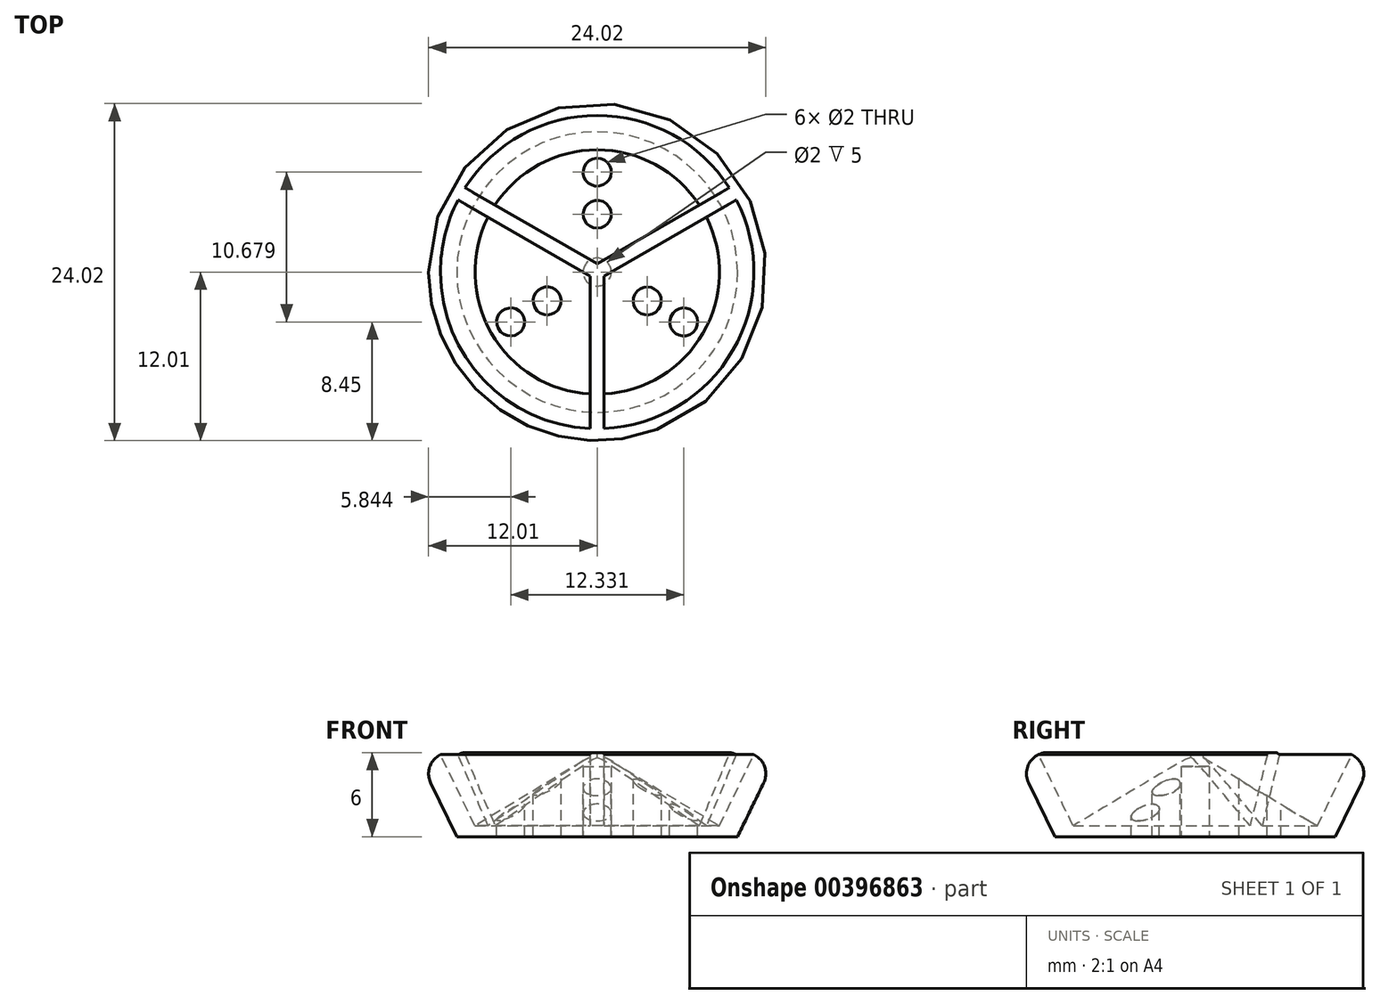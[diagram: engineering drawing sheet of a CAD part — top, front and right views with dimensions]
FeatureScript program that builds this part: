
annotation { "Feature Type Name" : "Feature", "Feature Type Description" : "" }
export const myFeature = defineFeature(function(context is Context, id is Id, definition is map)
    precondition{}
    {
        {
            var Q0;
            Q0=qCreatedBy(makeId("Front.planeOp"),FACE);
            var sketch = newSketch(context, id + "F0", { "sketchPlane" : qUnion([Q0])});
            skLineSegment(sketch, "E0", {"start": v(10, 0) * mm, "end": v(0, 6) * mm});
            skLineSegment(sketch, "E1", {"start": v(0, 6) * mm, "end": v(0, 0) * mm});
            skLineSegment(sketch, "E2", {"start": v(10, 0) * mm, "end": v(12.9, 6) * mm});
            skLineSegment(sketch, "E3", {"start": v(12.9, 6) * mm, "end": v(11.24, 6) * mm});
            skLineSegment(sketch, "E4", {"start": v(11.24, 6) * mm, "end": v(8.7, 0.77) * mm});
            skLineSegment(sketch, "E5", {"start": v(10, 0) * mm, "end": v(0, 0) * mm});
            skLineSegment(sketch, "E6", {"start": v(12.9, 6) * mm, "end": v(16.69, 6) * mm});
            skLineSegment(sketch, "E7", {"start": v(16.69, 6) * mm, "end": v(13.78, 0) * mm});
            skLineSegment(sketch, "E8", {"start": v(13.78, 0) * mm, "end": v(10, 0) * mm});
            skSolve(sketch);
        }
        {
            var Q0;
            {var subQ3=sQuery(id+"F0.wireOp",EDGE,"E1");Q0=makeQuery(id+"F0.imprint","IMPRINT",FACE,{"disambiguationData":[TD([[makeQuery(id+"F0.imprint","IMPRINT",EDGE,{"derivedFrom":subQ3}),1.0]])]});}
            var Q1;
            {var subQ0=sQuery(id+"F0.wireOp",EDGE,"E2");Q1=makeQuery(id+"F0.imprint","IMPRINT",FACE,{"disambiguationData":[TD([[makeQuery(id+"F0.imprint","IMPRINT",EDGE,{"derivedFrom":subQ0}),1.0]])]});}
            var Q2;
            Q2=sQuery(id+"F0.wireOp",EDGE,"E1");
            revolve(context, id + "F1", {"entities" : qUnion([Q0, Q1]), "axis" : qUnion([Q2]), "revolveType" : RevolveType.FULL});
        }
        {
            var Q0;
            Q0=makeQuery(id+"F1.opRevolve","SWEPT_FACE",FACE,{"disambiguationData":[OSD([sQuery(id+"F0.wireOp",EDGE,"E3")])]});
            var sketch = newSketch(context, id + "F2", { "sketchPlane" : qUnion([Q0])});
            skLineSegment(sketch, "E9", {"start": v(0, 0) * mm, "end": v(0, -12.9) * mm});
            skLineSegment(sketch, "E10", {"start": v(0, 0) * mm, "end": v(-11.18, 6.45) * mm});
            skLineSegment(sketch, "E11", {"start": v(0, 0) * mm, "end": v(11.18, 6.45) * mm});
            skLineSegment(sketch, "E12", {"start": v(-11.42, 6.01) * mm, "end": v(-0.5, -0.29) * mm});
            skLineSegment(sketch, "E13", {"start": v(-0.5, -0.29) * mm, "end": v(-0.5, -12.9) * mm});
            skLineSegment(sketch, "E14", {"start": v(-0.5, -12.9) * mm, "end": v(0.5, -12.9) * mm});
            skLineSegment(sketch, "E15", {"start": v(0.5, -12.9) * mm, "end": v(0.5, -0.29) * mm});
            skLineSegment(sketch, "E16", {"start": v(0.5, -0.29) * mm, "end": v(11.42, 6.01) * mm});
            skLineSegment(sketch, "E17", {"start": v(11.42, 6.01) * mm, "end": v(10.92, 6.88) * mm});
            skLineSegment(sketch, "E18", {"start": v(10.92, 6.88) * mm, "end": v(0, 0.58) * mm});
            skLineSegment(sketch, "E19", {"start": v(0, 0.58) * mm, "end": v(-10.92, 6.88) * mm});
            skLineSegment(sketch, "E20", {"start": v(-10.92, 6.88) * mm, "end": v(-11.42, 6.01) * mm});
            skCircle(sketch, "E21", {"center": v(0, 0) * mm, "radius": 11.24 * mm});
            skSolve(sketch);
        }
        {
            var Q0;
            {var subQ0=sQuery(id+"F2.wireOp",EDGE,"E13");var subQ1=sQuery(id+"F2.wireOp",EDGE,"E12");var subQ2=makeQuery(id+"F2.imprint","INTERSECT",VERTEX,{"derivedFrom":[subQ1,subQ0]});Q0=makeQuery(id+"F2.imprint","IMPRINT",FACE,{"disambiguationData":[TD([[makeQuery(id+"F2.imprint","IMPRINT",EDGE,{"disambiguationData":[TD([[subQ2,1.0]])],"derivedFrom":subQ1}),1.0]])]});}
            var Q1;
            {var subQ0=sQuery(id+"F2.wireOp",EDGE,"E16");var subQ1=sQuery(id+"F2.wireOp",EDGE,"E15");var subQ2=makeQuery(id+"F2.imprint","INTERSECT",VERTEX,{"derivedFrom":[subQ1,subQ0]});Q1=makeQuery(id+"F2.imprint","IMPRINT",FACE,{"disambiguationData":[TD([[makeQuery(id+"F2.imprint","IMPRINT",EDGE,{"disambiguationData":[TD([[subQ2,1.0]])],"derivedFrom":subQ1}),1.0]])]});}
            var Q2;
            {var subQ0=sQuery(id+"F2.wireOp",EDGE,"E19");var subQ1=sQuery(id+"F2.wireOp",EDGE,"E18");var subQ2=makeQuery(id+"F2.imprint","INTERSECT",VERTEX,{"derivedFrom":[subQ1,subQ0]});Q2=makeQuery(id+"F2.imprint","IMPRINT",FACE,{"disambiguationData":[TD([[makeQuery(id+"F2.imprint","IMPRINT",EDGE,{"disambiguationData":[TD([[subQ2,1.0]])],"derivedFrom":subQ1}),1.0]])]});}
            var Q3;
            Q3=makeQuery(id+"F1.opRevolve","SWEPT_FACE",FACE,{"disambiguationData":[OSD([sQuery(id+"F0.wireOp",EDGE,"E5")])]});
            extrude(context, id + "F3", {"entities" : qUnion([Q0, Q1, Q2]), "operationType" : NewBodyOperationType.ADD, "endBound" : BoundingType.UP_TO_SURFACE, "oppositeDirection" : true, "endBoundEntityFace" : qUnion([Q3]), "depth" : 25 * mm});
        }
        {
            var Q0;
            Q0=makeQuery(id+"F3.boolean.opBoolean","MERGE",FACE,{"derivedFrom":[makeQuery(id+"F1.opRevolve","SWEPT_FACE",FACE,{"disambiguationData":[OSD([sQuery(id+"F0.wireOp",EDGE,"E3")])]}),makeQuery(id+"F3.opExtrude","CAP_FACE",FACE,{"disambiguationData":[OSD([sQuery(id+"F2.wireOp",EDGE,"E12"),sQuery(id+"F2.wireOp",EDGE,"E13"),sQuery(id+"F2.wireOp",EDGE,"E15"),sQuery(id+"F2.wireOp",EDGE,"E16"),sQuery(id+"F2.wireOp",EDGE,"E18"),sQuery(id+"F2.wireOp",EDGE,"E19"),sQuery(id+"F2.wireOp",EDGE,"E21")])],"isStart":true})]});
            var sketch = newSketch(context, id + "F4", { "sketchPlane" : qUnion([Q0])});
            skLineSegment(sketch, "E22", {"start": v(0, 0) * mm, "end": v(9.73, -5.62) * mm});
            skLineSegment(sketch, "E23", {"start": v(0, 0) * mm, "end": v(-9.73, -5.62) * mm});
            skLineSegment(sketch, "E24", {"start": v(0, 0) * mm, "end": v(0, 11.24) * mm});
            skCircle(sketch, "E25", {"center": v(-3.57, -2.06) * mm, "radius": 1 * mm});
            skCircle(sketch, "E26", {"center": v(-6.17, -3.56) * mm, "radius": 1 * mm});
            skCircle(sketch, "E27", {"center": v(3.57, -2.06) * mm, "radius": 1 * mm});
            skCircle(sketch, "E28", {"center": v(6.17, -3.56) * mm, "radius": 1 * mm});
            skCircle(sketch, "E29", {"center": v(0, 7.12) * mm, "radius": 1 * mm});
            skCircle(sketch, "E30", {"center": v(0, 4.12) * mm, "radius": 1 * mm});
            skPoint(sketch, "E31", {"position": v(0, 5.62) * mm});
            skPoint(sketch, "E32", {"position": v(4.87, -2.8) * mm});
            skPoint(sketch, "E33", {"position": v(-4.87, -2.8) * mm});
            skSolve(sketch);
        }
        {
            var Q0;
            Q0 = qSketchRegion(id + "F4", true);
            extrude(context, id + "F5", {"entities" : qUnion([Q0]), "operationType" : NewBodyOperationType.REMOVE, "endBound" : BoundingType.THROUGH_ALL, "oppositeDirection" : true, "depth" : 25 * mm});
        }
        {
            var Q0;
            Q0=makeQuery(id+"F3.boolean.opBoolean","MERGE",FACE,{"derivedFrom":[makeQuery(id+"F1.opRevolve","SWEPT_FACE",FACE,{"disambiguationData":[OSD([sQuery(id+"F0.wireOp",EDGE,"E5")])]}),makeQuery(id+"F3.opExtrude","CAP_FACE",FACE,{"disambiguationData":[OSD([sQuery(id+"F2.wireOp",EDGE,"E12"),sQuery(id+"F2.wireOp",EDGE,"E13"),sQuery(id+"F2.wireOp",EDGE,"E15"),sQuery(id+"F2.wireOp",EDGE,"E16"),sQuery(id+"F2.wireOp",EDGE,"E18"),sQuery(id+"F2.wireOp",EDGE,"E19"),sQuery(id+"F2.wireOp",EDGE,"E21")])],"isStart":false})]});
            var sketch = newSketch(context, id + "F6", { "sketchPlane" : qUnion([Q0])});
            skCircle(sketch, "E34", {"center": v(0, 0) * mm, "radius": 1 * mm});
            skCircle(sketch, "E35", {"center": v(0, 6) * mm, "radius": 1.5 * mm});
            skSolve(sketch);
        }
        {
            var Q0;
            Q0=makeQuery(id+"F6.imprint","IMPRINT",FACE,{"disambiguationData":[TD([[makeQuery(id+"F6.imprint","IMPRINT",EDGE,{"derivedFrom":sQuery(id+"F6.wireOp",EDGE,"E34")}),1.0]])]});
            extrude(context, id + "F7", {"entities" : qUnion([Q0]), "operationType" : NewBodyOperationType.REMOVE, "oppositeDirection" : true, "depth" : 5 * mm});
        }
        {
            var Q0;
            Q0=makeQuery(id+"F1.opRevolve","SWEPT_EDGE",EDGE,{"disambiguationData":[OSD([sQuery(id+"F0.wireOp",EDGE,"E2"),sQuery(id+"F0.wireOp",EDGE,"E3")])]});
            fillet(context, id + "F8", {"entities" : qUnion([Q0]), "radius" : 1.5 * mm, "tangentPropagation" : true, "allowEdgeOverflow" : false});
        }
        {
            var Q0;
            Q0=makeQuery(id+"F0.imprint","IMPRINT",FACE,{"disambiguationData":[TD([[makeQuery(id+"F0.imprint","IMPRINT",EDGE,{"derivedFrom":sQuery(id+"F0.wireOp",EDGE,"E2")}),-1.0]])]});
            var Q1;
            Q1=sQuery(id+"F0.wireOp",EDGE,"E1");
            revolve(context, id + "F9", {"operationType" : NewBodyOperationType.REMOVE, "entities" : qUnion([Q0]), "axis" : qUnion([Q1]), "revolveType" : RevolveType.FULL, "oppositeDirection" : true});
        }
    });
